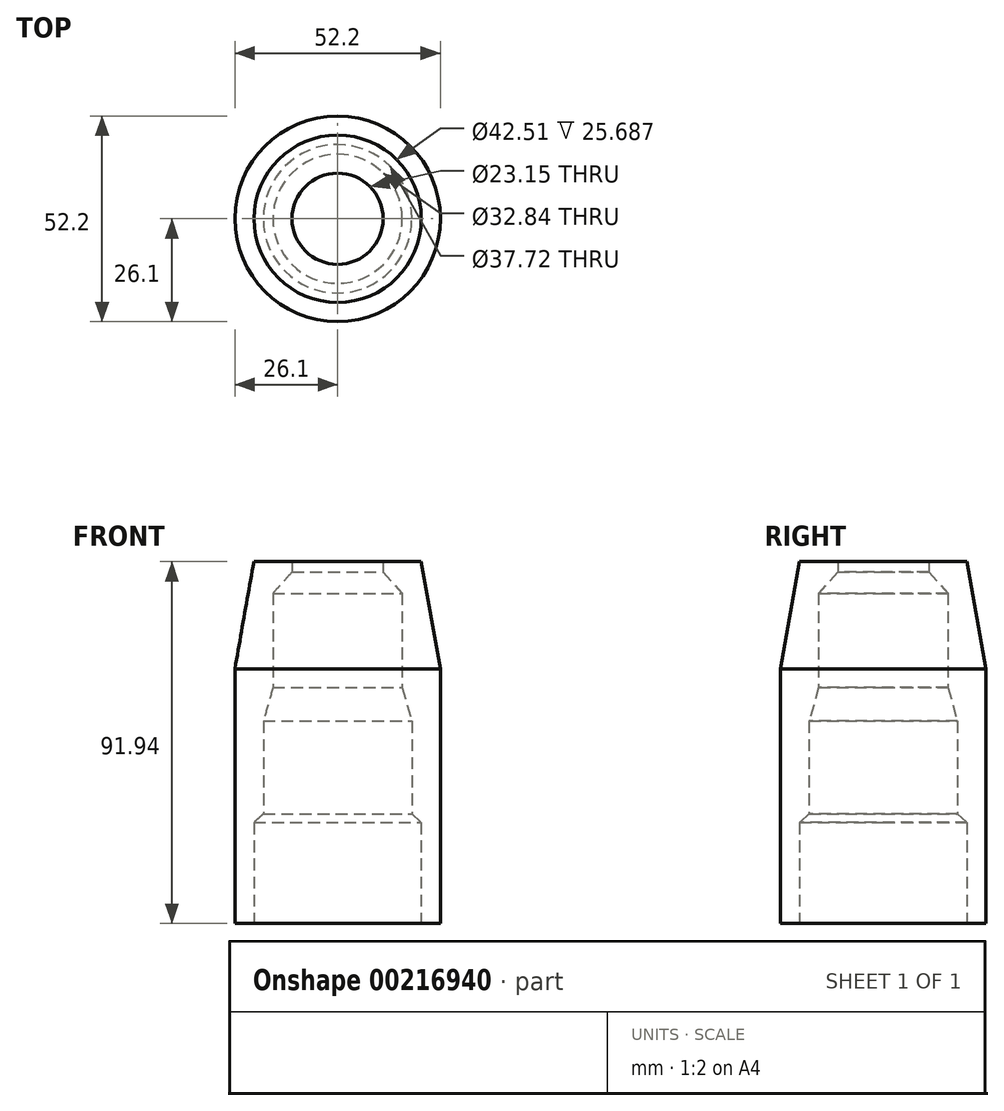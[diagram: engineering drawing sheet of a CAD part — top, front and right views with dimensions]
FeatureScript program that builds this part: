
annotation { "Feature Type Name" : "Feature", "Feature Type Description" : "" }
export const myFeature = defineFeature(function(context is Context, id is Id, definition is map)
    precondition{}
    {
        {
            var Q0;
            Q0=qCreatedBy(makeId("Front.planeOp"),FACE);
            var sketch = newSketch(context, id + "F0", { "sketchPlane" : qUnion([Q0])});
            skLineSegment(sketch, "E0", {"start": v(0, 0) * mm, "end": v(0, 91.94) * mm, "construction": true});
            skLineSegment(sketch, "E1", {"start": v(21.26, 0) * mm, "end": v(21.26, 25.69) * mm});
            skLineSegment(sketch, "E2", {"start": v(21.26, 25.69) * mm, "end": v(18.86, 27.84) * mm});
            skLineSegment(sketch, "E3", {"start": v(18.86, 27.84) * mm, "end": v(18.86, 51.4) * mm});
            skLineSegment(sketch, "E4", {"start": v(18.86, 51.4) * mm, "end": v(16.42, 59.96) * mm});
            skLineSegment(sketch, "E5", {"start": v(16.42, 59.96) * mm, "end": v(16.42, 83.9) * mm});
            skLineSegment(sketch, "E6", {"start": v(16.42, 83.9) * mm, "end": v(11.58, 89.3) * mm});
            skLineSegment(sketch, "E7", {"start": v(11.58, 89.3) * mm, "end": v(11.58, 91.94) * mm});
            skLineSegment(sketch, "E8", {"start": v(11.58, 91.94) * mm, "end": v(21.26, 91.94) * mm});
            skLineSegment(sketch, "E9", {"start": v(21.26, 91.94) * mm, "end": v(26.1, 64.7) * mm});
            skLineSegment(sketch, "E10", {"start": v(26.1, 64.7) * mm, "end": v(26.1, 0) * mm});
            skLineSegment(sketch, "E11", {"start": v(26.1, 0) * mm, "end": v(21.26, 0) * mm});
            skSolve(sketch);
        }
        {
            var Q0;
            Q0 = qSketchRegion(id + "F0", true);
            var Q1;
            Q1=sQuery(id+"F0.wireOp",EDGE,"E0");
            revolve(context, id + "F1", {"entities" : qUnion([Q0]), "axis" : qUnion([Q1]), "revolveType" : RevolveType.FULL});
        }
    });
